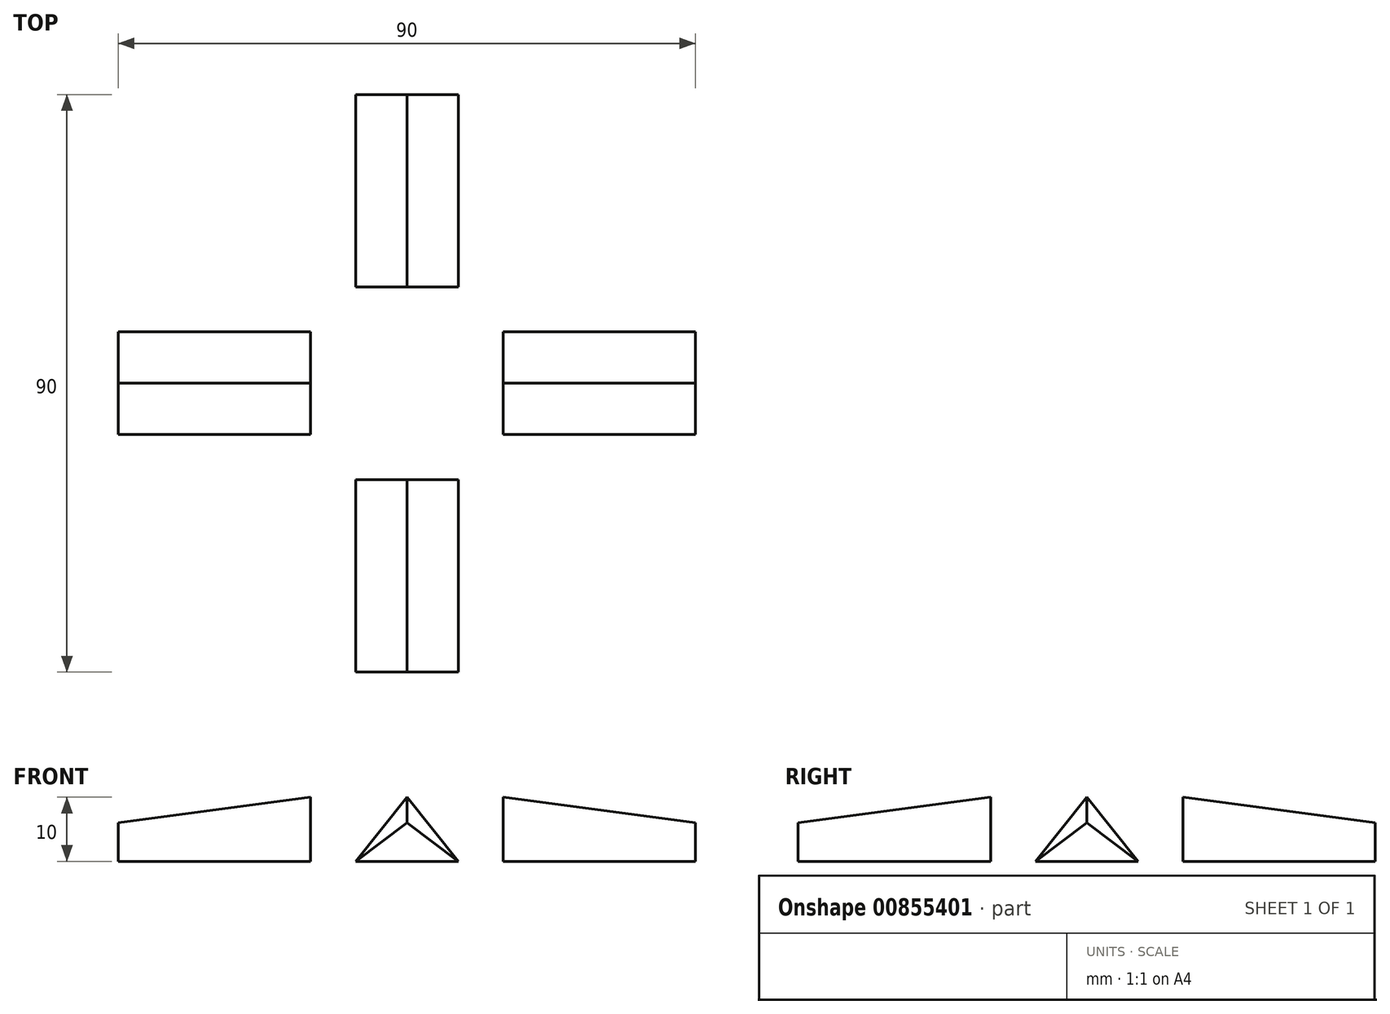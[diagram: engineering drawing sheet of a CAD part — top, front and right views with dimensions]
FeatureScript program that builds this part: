
annotation { "Feature Type Name" : "Feature", "Feature Type Description" : "" }
export const myFeature = defineFeature(function(context is Context, id is Id, definition is map)
    precondition{}
    {
        {
            var Q0;
            Q0=qCreatedBy(makeId("Front.planeOp"),FACE);
            cPlane(context, id + "F0", {"entities" : qUnion([Q0]), "cplaneType" : CPlaneType.OFFSET, "offset" : 45 * mm, "width" : 150 * mm, "height" : 150 * mm});
        }
        {
            var Q0;
            Q0=qCreatedBy(id+"F0.planeOp",FACE);
            var sketch = newSketch(context, id + "F1", { "sketchPlane" : qUnion([Q0])});
            skLineSegment(sketch, "E0", {"start": v(-8, 0) * mm, "end": v(8, 0) * mm});
            skLineSegment(sketch, "E1", {"start": v(8, 0) * mm, "end": v(0, 6) * mm});
            skLineSegment(sketch, "E2", {"start": v(0, 6) * mm, "end": v(-8, 0) * mm});
            skSolve(sketch);
        }
        {
            var Q0;
            Q0=qCreatedBy(makeId("Front.planeOp"),FACE);
            cPlane(context, id + "F2", {"entities" : qUnion([Q0]), "cplaneType" : CPlaneType.OFFSET, "offset" : 15 * mm, "width" : 150 * mm, "height" : 150 * mm});
        }
        {
            var Q0;
            Q0=qCreatedBy(id+"F2.planeOp",FACE);
            var sketch = newSketch(context, id + "F3", { "sketchPlane" : qUnion([Q0])});
            skLineSegment(sketch, "E3", {"start": v(-8, 0) * mm, "end": v(8, 0) * mm});
            skLineSegment(sketch, "E4", {"start": v(8, 0) * mm, "end": v(0, 10) * mm});
            skLineSegment(sketch, "E5", {"start": v(0, 10) * mm, "end": v(-8, 0) * mm});
            skSolve(sketch);
        }
        {
            var Q0;
            Q0 = qSketchRegion(id + "F1", true);
            var Q1;
            Q1 = qSketchRegion(id + "F3", true);
            loft(context, id + "F4", {"sheetProfilesArray" : [{ "sheetProfileEntities" : qUnion([Q0]) }, { "sheetProfileEntities" : qUnion([Q1]) }]});
        }
        {
            var Q0;
            Q0=makeQuery(id+"F4.opLoft","SWEPT_BODY",BODY,{"disambiguationData":[OSD([makeQuery(id+"F1.imprint","IMPRINT",FACE,{"disambiguationData":[TD([[makeQuery(id+"F1.imprint","IMPRINT",EDGE,{"derivedFrom":sQuery(id+"F1.wireOp",EDGE,"E0")}),1.0]])]}),makeQuery(id+"F3.imprint","IMPRINT",FACE,{"disambiguationData":[TD([[makeQuery(id+"F3.imprint","IMPRINT",EDGE,{"derivedFrom":sQuery(id+"F3.wireOp",EDGE,"E3")}),1.0]])]})])]});
            var Q1;
            Q1=qCreatedBy(makeId("Front.planeOp"),FACE);
            mirror(context, id + "F5", {"entities" : qUnion([Q0]), "mirrorPlane" : qUnion([Q1])});
        }
        {
            var Q0;
            Q0=qCreatedBy(makeId("Front.planeOp"),FACE);
            var sketch = newSketch(context, id + "F6", { "sketchPlane" : qUnion([Q0])});
            skLineSegment(sketch, "E6", {"start": v(0, 68.84) * mm, "end": v(0, -26.46) * mm, "construction": true});
            skSolve(sketch);
        }
        {
            var Q0;
            Q0=sQuery(id+"F6.wireOp",EDGE,"E6");
            cPlane(context, id + "F7", {"entities" : qUnion([Q0]), "cplaneType" : CPlaneType.LINE_ANGLE, "offset" : 25 * mm, "angle" : 45 * degree, "width" : 150 * mm, "height" : 150 * mm});
        }
        {
            var Q0;
            Q0=makeQuery(id+"F4.opLoft","SWEPT_BODY",BODY,{"disambiguationData":[OSD([makeQuery(id+"F1.imprint","IMPRINT",FACE,{"disambiguationData":[TD([[makeQuery(id+"F1.imprint","IMPRINT",EDGE,{"derivedFrom":sQuery(id+"F1.wireOp",EDGE,"E0")}),1.0]])]}),makeQuery(id+"F3.imprint","IMPRINT",FACE,{"disambiguationData":[TD([[makeQuery(id+"F3.imprint","IMPRINT",EDGE,{"derivedFrom":sQuery(id+"F3.wireOp",EDGE,"E3")}),1.0]])]})])]});
            var Q1;
            Q1=makeQuery(id+"F5.opPattern","COPY",BODY,{"derivedFrom":makeQuery(id+"F4.opLoft","SWEPT_BODY",BODY,{"disambiguationData":[OSD([makeQuery(id+"F1.imprint","IMPRINT",FACE,{"disambiguationData":[TD([[makeQuery(id+"F1.imprint","IMPRINT",EDGE,{"derivedFrom":sQuery(id+"F1.wireOp",EDGE,"E0")}),1.0]])]}),makeQuery(id+"F3.imprint","IMPRINT",FACE,{"disambiguationData":[TD([[makeQuery(id+"F3.imprint","IMPRINT",EDGE,{"derivedFrom":sQuery(id+"F3.wireOp",EDGE,"E3")}),1.0]])]})])]}),"instanceName":"1"});
            var Q2;
            Q2=qCreatedBy(id+"F7.planeOp",FACE);
            mirror(context, id + "F8", {"entities" : qUnion([Q0, Q1]), "mirrorPlane" : qUnion([Q2])});
        }
    });
